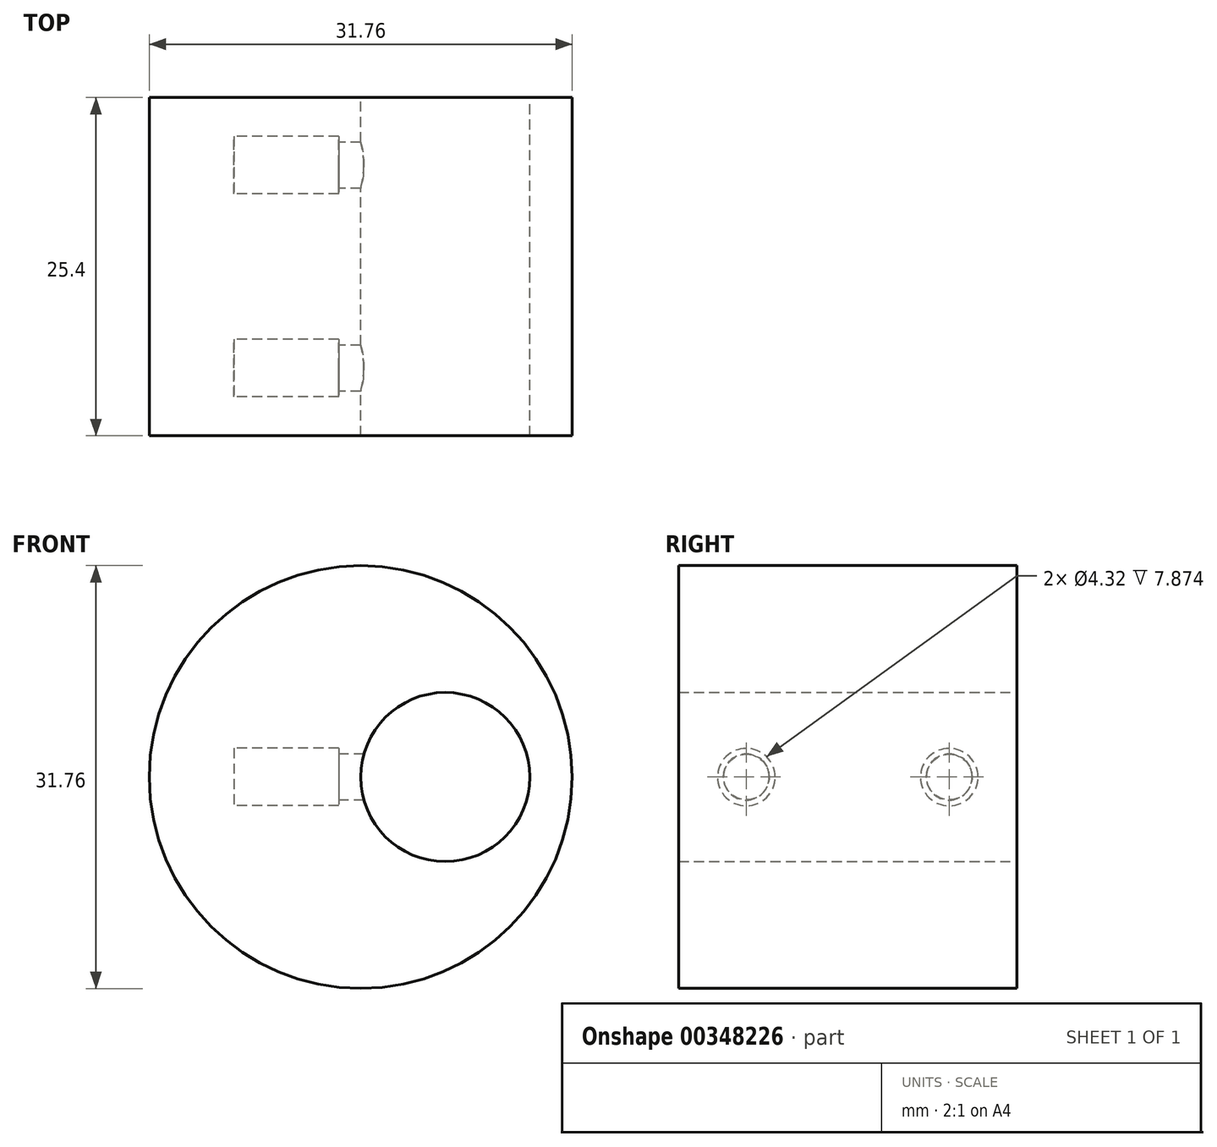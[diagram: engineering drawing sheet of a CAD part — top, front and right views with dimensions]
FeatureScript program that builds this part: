
annotation { "Feature Type Name" : "Feature", "Feature Type Description" : "" }
export const myFeature = defineFeature(function(context is Context, id is Id, definition is map)
    precondition{}
    {
        {
            var Q0;
            Q0=qCreatedBy(makeId("Front.planeOp"),FACE);
            var sketch = newSketch(context, id + "F0", { "sketchPlane" : qUnion([Q0])});
            skCircle(sketch, "E0", {"center": v(-6.35, 0) * mm, "radius": 15.88 * mm});
            skCircle(sketch, "E1", {"center": v(0, 0) * mm, "radius": 6.35 * mm});
            skSolve(sketch);
        }
        {
            var Q0;
            Q0=qSketchRegion(id+"F0",true);
            extrude(context, id + "F1", {"entities" : qUnion([Q0]), "endBound" : BoundingType.SYMMETRIC, "depth" : 25.4 * mm});
        }
        {
            var Q0;
            Q0=qCreatedBy(makeId("Right.planeOp"),FACE);
            cPlane(context, id + "F2", {"entities" : qUnion([Q0]), "cplaneType" : CPlaneType.OFFSET, "offset" : 15.88 * mm, "oppositeDirection" : true, "width" : 152.4 * mm, "height" : 152.4 * mm});
        }
        {
            var Q0;
            Q0=qCreatedBy(id+"F2.planeOp",FACE);
            var sketch = newSketch(context, id + "F3", { "sketchPlane" : qUnion([Q0])});
            skPoint(sketch, "E2", {"position": v(7.62, 0) * mm});
            skPoint(sketch, "E3", {"position": v(-7.62, 0) * mm});
            skSolve(sketch);
        }
        {
            var Q0;
            Q0=sQuery(id+"F3.wireOp",VERTEX,"E2");
            var Q1;
            Q1=sQuery(id+"F3.wireOp",VERTEX,"E3");
            var Q2;
            Q2=makeQuery(id+"F1.opExtrude","SWEPT_BODY",BODY,{"disambiguationData":[OSD([sQuery(id+"F0.wireOp",EDGE,"E0"),sQuery(id+"F0.wireOp",EDGE,"E1")])]});
            hole(context, id + "F4", {"style" : HoleStyle.C_BORE, "holeDiameter" : 3.45 * mm, "cBoreDiameter" : 4.32 * mm, "cBoreDepth" : 7.87 * mm, "endStyle" : HoleEndStyle.BLIND, "oppositeDirection" : true, "holeDepth" : 19.05 * mm, "locations" : qUnion([Q0, Q1]), "scope" : qUnion([Q2])});
        }
    });
